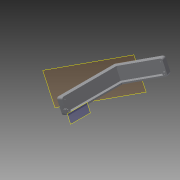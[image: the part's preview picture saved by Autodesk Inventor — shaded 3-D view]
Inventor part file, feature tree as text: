
AUTODESK INVENTOR PART (.ipt)
format: ipt  version: 2014 SP2 (Build 180247200, 247)  size: 188,416 bytes
history: native  units: mm
features: extrude x6, sketch x6, other x4
ambient origin geometry x8: Origin, YZ Plane, XZ Plane, XY Plane, X Axis, Y Axis, Z Axis, Center Point
bodies: Body1 (feature_tree)
feature tree (16):
  other  "camera-holder.ipt"
  extrude  "押し出し1"  Depth=10.0mm
  extrude  "押し出し2"  Depth=1.5mm TaperAngle=0.0deg
  sketch  "スケッチ5"
  sketch  "スケッチ6"
  extrude  "押し出し3"  Depth=1.5mm TaperAngle=0.0deg
  extrude  "押し出し4"  Depth=3.0mm
  extrude  "押し出し5"  Depth=3.0mm
  extrude  "押し出し6"  Depth=3.0mm
  other  "ソリッド2::camera-holder.ipt"
  other  "TaggingFeature1"
  sketch  "スケッチ21"
  sketch  "スケッチ22"
  sketch  "スケッチ3"
  sketch  "スケッチ4"
  other  "ソリッド1"
